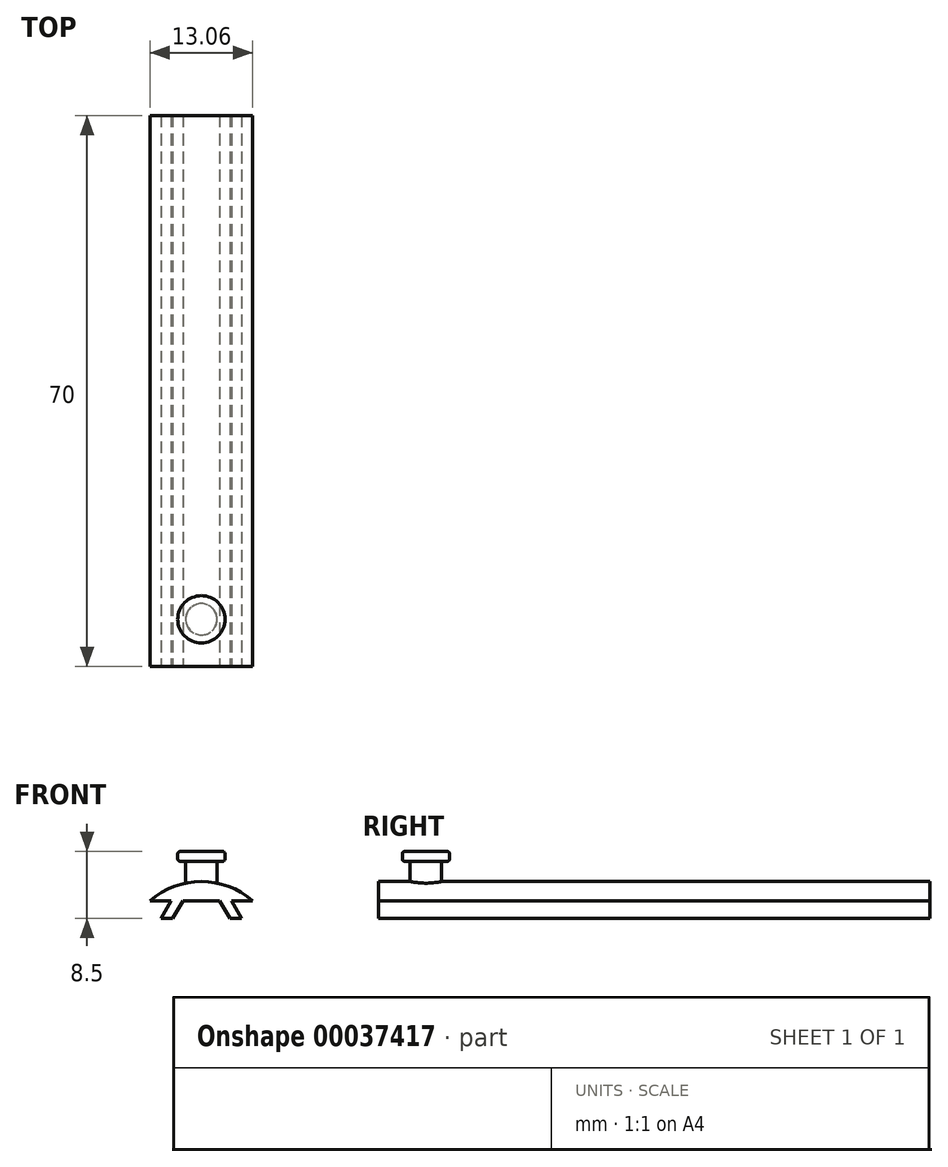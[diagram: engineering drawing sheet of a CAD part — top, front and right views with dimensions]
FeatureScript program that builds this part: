
annotation { "Feature Type Name" : "Feature", "Feature Type Description" : "" }
export const myFeature = defineFeature(function(context is Context, id is Id, definition is map)
    precondition{}
    {
        {
            var Q0;
            Q0=qCreatedBy(makeId("Front.planeOp"),FACE);
            var sketch = newSketch(context, id + "F0", { "sketchPlane" : qUnion([Q0])});
            skArc(sketch, "E0", {"start": v(6.53, 7.57) * mm, "mid": v(0, 10) * mm, "end": v(-6.53, 7.57) * mm});
            skLineSegment(sketch, "E1", {"start": v(-5.13, 5.32) * mm, "end": v(-3.83, 7.57) * mm});
            skLineSegment(sketch, "E2", {"start": v(-3.83, 7.57) * mm, "end": v(-6.53, 7.57) * mm});
            skLineSegment(sketch, "E3", {"start": v(-5.13, 5.32) * mm, "end": v(-3.63, 5.32) * mm});
            skLineSegment(sketch, "E4", {"start": v(-3.63, 5.32) * mm, "end": v(-2.33, 7.57) * mm});
            skLineSegment(sketch, "E5", {"start": v(-2.33, 7.57) * mm, "end": v(0, 7.57) * mm});
            skLineSegment(sketch, "E6.MirrorCS", {"start": v(3.83, 7.57) * mm, "end": v(6.53, 7.57) * mm});
            skLineSegment(sketch, "E7.MirrorCS", {"start": v(2.33, 7.57) * mm, "end": v(0, 7.57) * mm});
            skLineSegment(sketch, "E8.MirrorCS", {"start": v(5.13, 5.32) * mm, "end": v(3.83, 7.57) * mm});
            skLineSegment(sketch, "E9.MirrorCS", {"start": v(5.13, 5.32) * mm, "end": v(3.63, 5.32) * mm});
            skLineSegment(sketch, "E10.MirrorCS", {"start": v(3.63, 5.32) * mm, "end": v(2.33, 7.57) * mm});
            skPoint(sketch, "E11.end.orphan", {"position": v(-5.74, 4.27) * mm});
            skPoint(sketch, "E12.start.orphan", {"position": v(-9.5, 3.12) * mm});
            skSolve(sketch);
        }
        {
            var Q0;
            Q0=makeQuery(id+"F0.imprint","IMPRINT",FACE,{"disambiguationData":[TD([[makeQuery(id+"F0.imprint","IMPRINT",EDGE,{"derivedFrom":sQuery(id+"F0.wireOp",EDGE,"E0")}),1.0]])]});
            extrude(context, id + "F1", {"entities" : qUnion([Q0]), "oppositeDirection" : true, "depth" : 70 * mm});
        }
        {
            var Q0;
            Q0=makeQuery(id+"F1.opExtrude","SWEPT_FACE",FACE,{"disambiguationData":[OSD([sQuery(id+"F0.wireOp",EDGE,"E5"),sQuery(id+"F0.wireOp",EDGE,"E7.MirrorCS")])]});
            var sketch = newSketch(context, id + "F2", { "sketchPlane" : qUnion([Q0])});
            skCircle(sketch, "E13", {"center": v(0, -6) * mm, "radius": 2 * mm});
            skSolve(sketch);
        }
        {
            var Q0;
            Q0=makeQuery(id+"F2.imprint","IMPRINT",FACE,{"disambiguationData":[TD([[makeQuery(id+"F2.imprint","IMPRINT",EDGE,{"derivedFrom":sQuery(id+"F2.wireOp",EDGE,"E13")}),1.0]])]});
            extrude(context, id + "F3", {"entities" : qUnion([Q0]), "operationType" : NewBodyOperationType.ADD, "oppositeDirection" : true, "depth" : 5 * mm});
        }
        {
            var Q0;
            Q0=makeQuery(id+"F3.opExtrude","CAP_FACE",FACE,{"disambiguationData":[OSD([sQuery(id+"F2.wireOp",EDGE,"E13")])],"isStart":false});
            var sketch = newSketch(context, id + "F4", { "sketchPlane" : qUnion([Q0])});
            skCircle(sketch, "E14", {"center": v(0, 6) * mm, "radius": 3 * mm});
            skSolve(sketch);
        }
        {
            var Q0;
            Q0 = qSketchRegion(id + "F4", true);
            extrude(context, id + "F5", {"entities" : qUnion([Q0]), "operationType" : NewBodyOperationType.ADD, "depth" : 1.25 * mm});
        }
        {
            var Q0;
            Q0=makeQuery(id+"F5.opExtrude","CAP_EDGE",EDGE,{"disambiguationData":[OSD([sQuery(id+"F4.wireOp",EDGE,"E14")])],"isStart":false});
            var Q1;
            Q1=makeQuery(id+"F5.opExtrude","CAP_EDGE",EDGE,{"disambiguationData":[OSD([sQuery(id+"F4.wireOp",EDGE,"E14")])],"isStart":true});
            fillet(context, id + "F6", {"entities" : qUnion([Q0, Q1]), "radius" : .3 * mm, "tangentPropagation" : true, "allowEdgeOverflow" : false});
        }
    });
